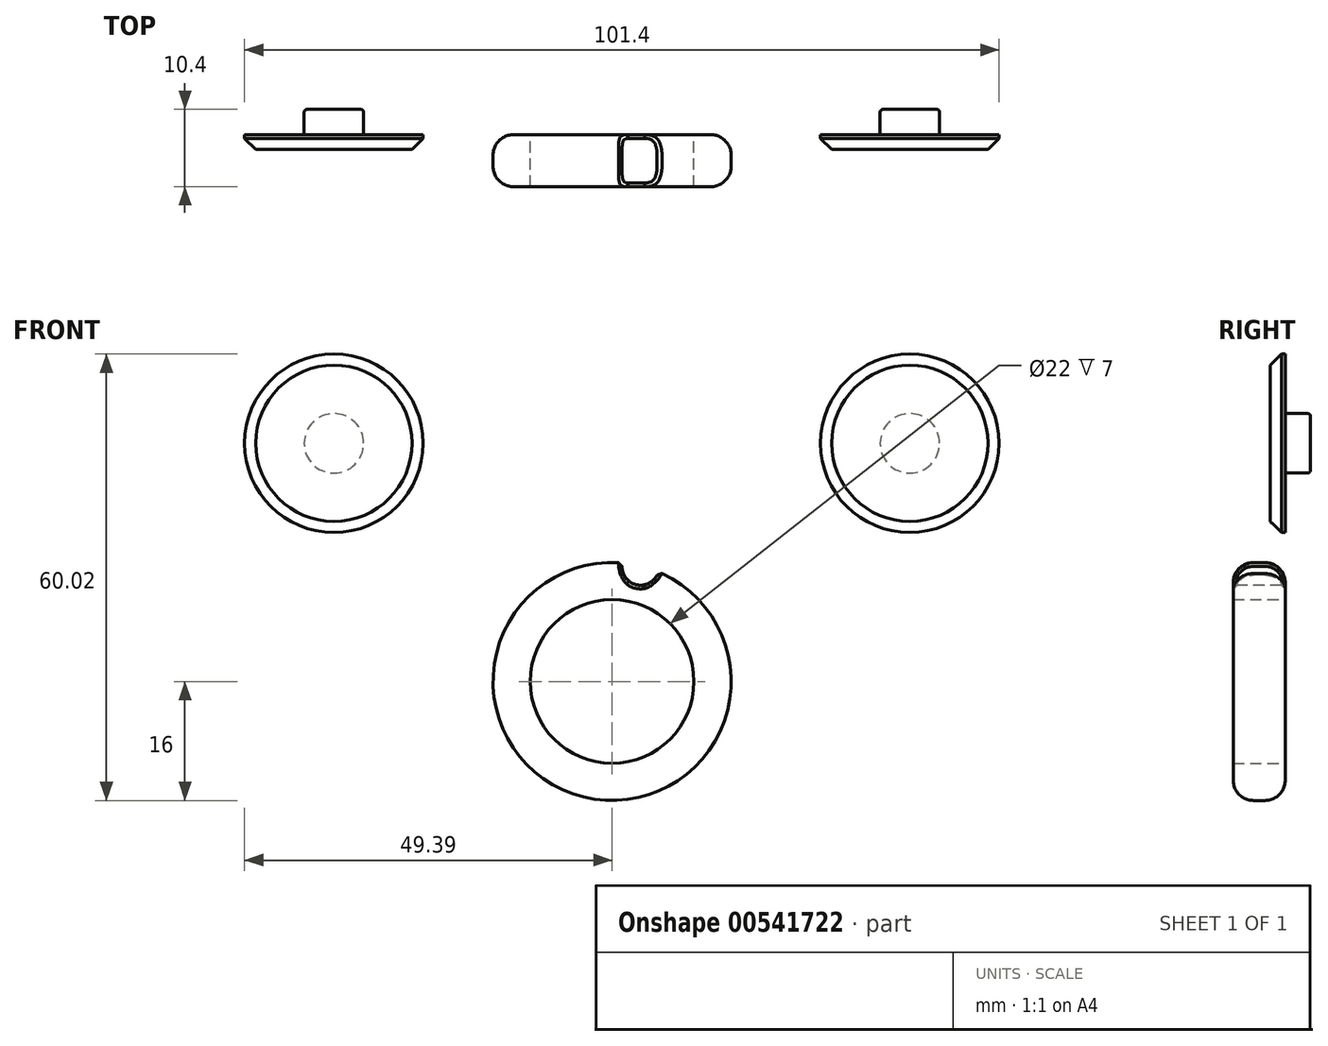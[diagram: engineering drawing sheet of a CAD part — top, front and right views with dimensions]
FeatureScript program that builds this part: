
annotation { "Feature Type Name" : "Feature", "Feature Type Description" : "" }
export const myFeature = defineFeature(function(context is Context, id is Id, definition is map)
    precondition{}
    {
        {
            var Q0;
            Q0=qCreatedBy(makeId("Front.planeOp"),FACE);
            var sketch = newSketch(context, id + "F0", { "sketchPlane" : qUnion([Q0])});
            skCircle(sketch, "E0", {"center": v(0, 0) * mm, "radius": 11 * mm});
            skCircle(sketch, "E1.0", {"center": v(0, 0) * mm, "radius": 16 * mm});
            skSolve(sketch);
        }
        {
            var Q0;
            Q0=makeQuery(id+"F0.imprint","IMPRINT",FACE,{"disambiguationData":[TD([[makeQuery(id+"F0.imprint","IMPRINT",EDGE,{"derivedFrom":sQuery(id+"F0.wireOp",EDGE,"E0")}),-1.0]])]});
            extrude(context, id + "F1", {"entities" : qUnion([Q0]), "depth" : 7 * mm, "offsetDistance" : 25 * mm});
        }
        {
            var Q0;
            Q0=makeQuery(id+"F1.opExtrude","CAP_EDGE",EDGE,{"disambiguationData":[OSD([sQuery(id+"F0.wireOp",EDGE,"E1.0")])],"isStart":false});
            var Q1;
            Q1=makeQuery(id+"F1.opExtrude","CAP_EDGE",EDGE,{"disambiguationData":[OSD([sQuery(id+"F0.wireOp",EDGE,"E1.0")])],"isStart":true});
            fillet(context, id + "F2", {"entities" : qUnion([Q0, Q1]), "radius" : 2.75 * mm, "tangentPropagation" : true, "allowEdgeOverflow" : false});
        }
        {
            var Q0;
            Q0=makeQuery(id+"F1.opExtrude","CAP_FACE",FACE,{"disambiguationData":[OSD([sQuery(id+"F0.wireOp",EDGE,"E0"),sQuery(id+"F0.wireOp",EDGE,"E1.0")])],"isStart":false});
            var sketch = newSketch(context, id + "F3", { "sketchPlane" : qUnion([Q0])});
            skCircle(sketch, "E2", {"center": v(3.83, 15.43) * mm, "radius": 2.49 * mm});
            skSolve(sketch);
        }
        {
            var Q0;
            Q0 = qSketchRegion(id + "F3", true);
            extrude(context, id + "F4", {"entities" : qUnion([Q0]), "operationType" : NewBodyOperationType.REMOVE, "oppositeDirection" : true, "depth" : 25 * mm, "offsetDistance" : 25 * mm});
        }
        {
            var Q0;
            Q0=makeQuery(id+"F4.boolean.opBoolean","COPY",FACE,{"derivedFrom":makeQuery(id+"F4.opExtrude","SWEPT_FACE",FACE,{"disambiguationData":[OSD([sQuery(id+"F3.wireOp",EDGE,"E2")])]})});
            chamfer(context, id + "F5", {"entities" : qUnion([Q0]), "width" : 0.5 * mm, "tangentPropagation" : true});
        }
        {
            var Q0;
            Q0=qCreatedBy(makeId("Front.planeOp"),FACE);
            var sketch = newSketch(context, id + "F6", { "sketchPlane" : qUnion([Q0])});
            skCircle(sketch, "E3", {"center": v(-37.39, 32.02) * mm, "radius": 12 * mm});
            skSolve(sketch);
        }
        {
            var Q0;
            Q0=makeQuery(id+"F6.imprint","IMPRINT",FACE,{"disambiguationData":[TD([[makeQuery(id+"F6.imprint","IMPRINT",EDGE,{"derivedFrom":sQuery(id+"F6.wireOp",EDGE,"E3")}),1.0]])]});
            extrude(context, id + "F7", {"entities" : qUnion([Q0]), "depth" : 2 * mm, "offsetDistance" : 25 * mm});
        }
        {
            var Q0;
            Q0=makeQuery(id+"F7.opExtrude","CAP_EDGE",EDGE,{"disambiguationData":[OSD([sQuery(id+"F6.wireOp",EDGE,"E3")])],"isStart":false});
            chamfer(context, id + "F8", {"entities" : qUnion([Q0]), "width" : 1.5 * mm, "tangentPropagation" : true});
        }
        {
            var Q0;
            Q0=makeQuery(id+"F7.opExtrude","CAP_FACE",FACE,{"disambiguationData":[OSD([sQuery(id+"F6.wireOp",EDGE,"E3")])],"isStart":true});
            var sketch = newSketch(context, id + "F9", { "sketchPlane" : qUnion([Q0])});
            skCircle(sketch, "E4", {"center": v(37.39, 32.02) * mm, "radius": 4 * mm});
            skSolve(sketch);
        }
        {
            var Q0;
            Q0 = qSketchRegion(id + "F9", true);
            extrude(context, id + "F10", {"entities" : qUnion([Q0]), "operationType" : NewBodyOperationType.ADD, "depth" : 3.4 * mm, "offsetDistance" : 25 * mm});
        }
        {
            var Q0;
            Q0=makeQuery(id+"F10.opExtrude","CAP_EDGE",EDGE,{"disambiguationData":[OSD([sQuery(id+"F9.wireOp",EDGE,"E4")])],"isStart":false});
            fillet(context, id + "F11", {"entities" : qUnion([Q0]), "radius" : 0.4 * mm, "tangentPropagation" : true, "allowEdgeOverflow" : false});
        }
        {
            var Q0;
            Q0=makeQuery(id+"F7.opExtrude","SWEPT_BODY",BODY,{"disambiguationData":[OSD([sQuery(id+"F6.wireOp",EDGE,"E3")])]});
            transform(context, id + "F12", {"entities" : qUnion([Q0]), "transformType" : TransformType.TRANSLATION_3D, "dx" : 77.4 * mm, "dy" : 0 * mm, "dz" : 0 * mm, "makeCopy" : true});
        }
    });
